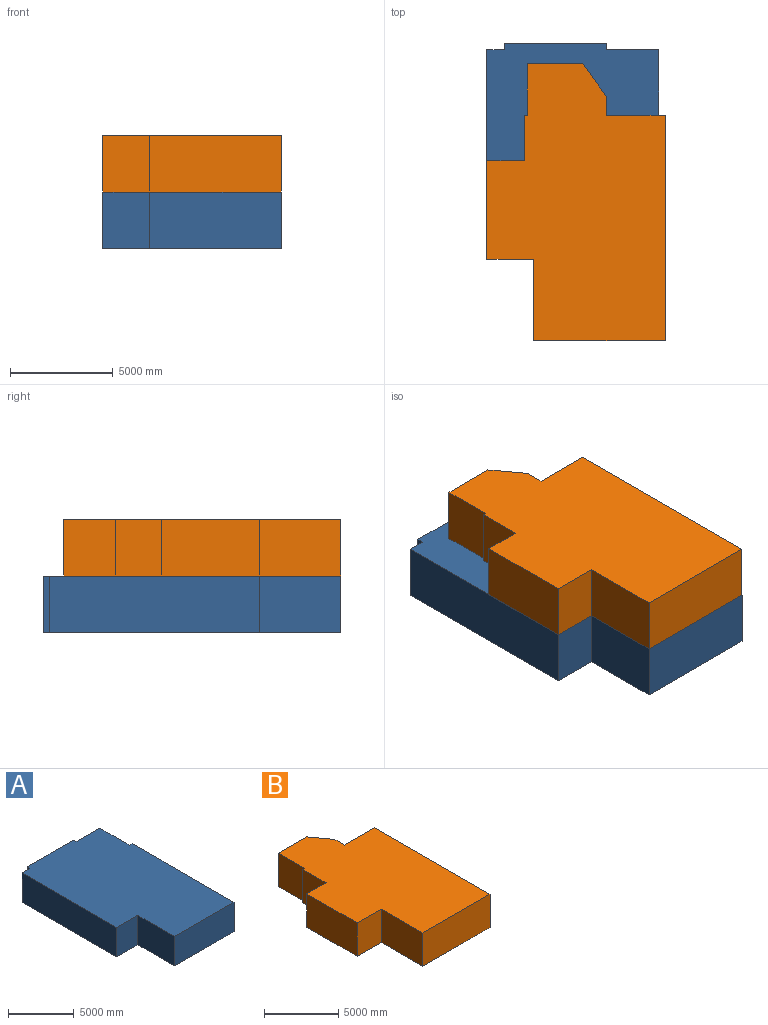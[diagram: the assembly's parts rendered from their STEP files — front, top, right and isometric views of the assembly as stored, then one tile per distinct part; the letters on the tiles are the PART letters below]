
ASSEMBLY  parts=2 mates=1
PART A: 14 faces, bbox 8686.8x14478x2743.2 mm
  f0: plane 3962.4x2743.2mm, normal (-1,0,0), area 10869655.7mm2, adj f1,f11,f12,f13
  f1: plane 6400.8x2743.2mm, normal (0,-1,0), area 17558674.6mm2, adj f0,f2,f12,f13
  f2: plane 10972.8x2743.2mm, normal (1,0,0), area 30100585mm2, adj f1,f3,f12,f13
  f3: plane 2743.2x304.8mm, normal (0,1,0), area 836127.4mm2, adj f2,f4,f12,f13
  f4: plane 3200.4x2743.2mm, normal (1,0,0), area 8779337.3mm2, adj f3,f5,f12,f13
  f5: plane 2743.2x2560.32mm, normal (0,1,0), area 7023469.8mm2, adj f4,f6,f12,f13
  f6: plane 2743.2x304.8mm, normal (1,0,0), area 836127.4mm2, adj f5,f7,f12,f13
  f7: plane 4968.24x2743.2mm, normal (0,1,0), area 13628876mm2, adj f6,f8,f12,f13
  f8: plane 2743.2x304.8mm, normal (-1,0,0), area 836127.4mm2, adj f7,f9,f12,f13
  f9: plane 2743.2x853.44mm, normal (0,1,0), area 2341156.6mm2, adj f8,f10,f12,f13
  f10: plane 10210.8x2743.2mm, normal (-1,0,0), area 28010266.6mm2, adj f9,f11,f12,f13
  f11: plane 2743.2x2286mm, normal (0,-1,0), area 6270955.2mm2, adj f0,f10,f12,f13
  f12: plane 14478x8686.8mm, normal (0,0,1), area 114600545mm2, adj f0,f1,f2,f3,f4,f5,f6,f7
  f13: plane 14478x8686.8mm, normal (0,0,-1), area 114600545mm2, adj f0,f1,f2,f3,f4,f5,f6,f7
PART B: 15 faces, bbox 8686.8x13472.2x2743.2 mm
  f0: plane 3962.4x2743.2mm, normal (-1,0,0), area 10869655.7mm2, adj f1,f12,f13,f14
  f1: plane 6400.8x2743.2mm, normal (0,-1,0), area 17558674.6mm2, adj f0,f2,f13,f14
  f2: plane 10972.8x2743.2mm, normal (1,0,0), area 30100585mm2, adj f1,f3,f13,f14
  f3: plane 2865.12x2743.2mm, normal (0,1,0), area 7859597.2mm2, adj f2,f4,f13,f14
  f4: plane 2743.2x929.71mm, normal (1,0,0), area 2550391.4mm2, adj f3,f5,f13,f14
  f5: plane 2743.2x1569.65mm, normal (0.8,0.59,0), area 5351215.1mm2, adj f4,f6,f13,f14
  f6: plane 2743.2x2682.24mm, normal (0,1,0), area 7357920.8mm2, adj f5,f7,f13,f14
  f7: plane 2743.2x2499.36mm, normal (-1,0,0), area 6856244.4mm2, adj f6,f8,f13,f14
  f8: plane 2743.2x152.4mm, normal (0,1,0), area 418063.7mm2, adj f7,f9,f13,f14
  f9: plane 2743.2x2225.04mm, normal (-1,0,0), area 6103729.7mm2, adj f8,f10,f13,f14
  f10: plane 2743.2x1828.8mm, normal (0,1,0), area 5016764.2mm2, adj f9,f11,f13,f14
  f11: plane 4785.36x2743.2mm, normal (-1,0,0), area 13127199.6mm2, adj f10,f12,f13,f14
  f12: plane 2743.2x2286mm, normal (0,-1,0), area 6270955.2mm2, adj f0,f11,f13,f14
  f13: plane 13472.16x8686.8mm, normal (0,0,1), area 90881048.2mm2, adj f0,f1,f2,f3,f4,f5,f6,f7
  f14: plane 13472.16x8686.8mm, normal (0,0,-1), area 90881048.2mm2, adj f0,f1,f2,f3,f4,f5,f6,f7
PLACE A t=(-1089.01,-201.82,90.76)mm
PLACE B t=(232.01,2414.99,2833.96)mm
MATE fastened B.f14 <-> A.f12  axis (0,0,1) through (3646.24,-4309.57,2833.96)mm
